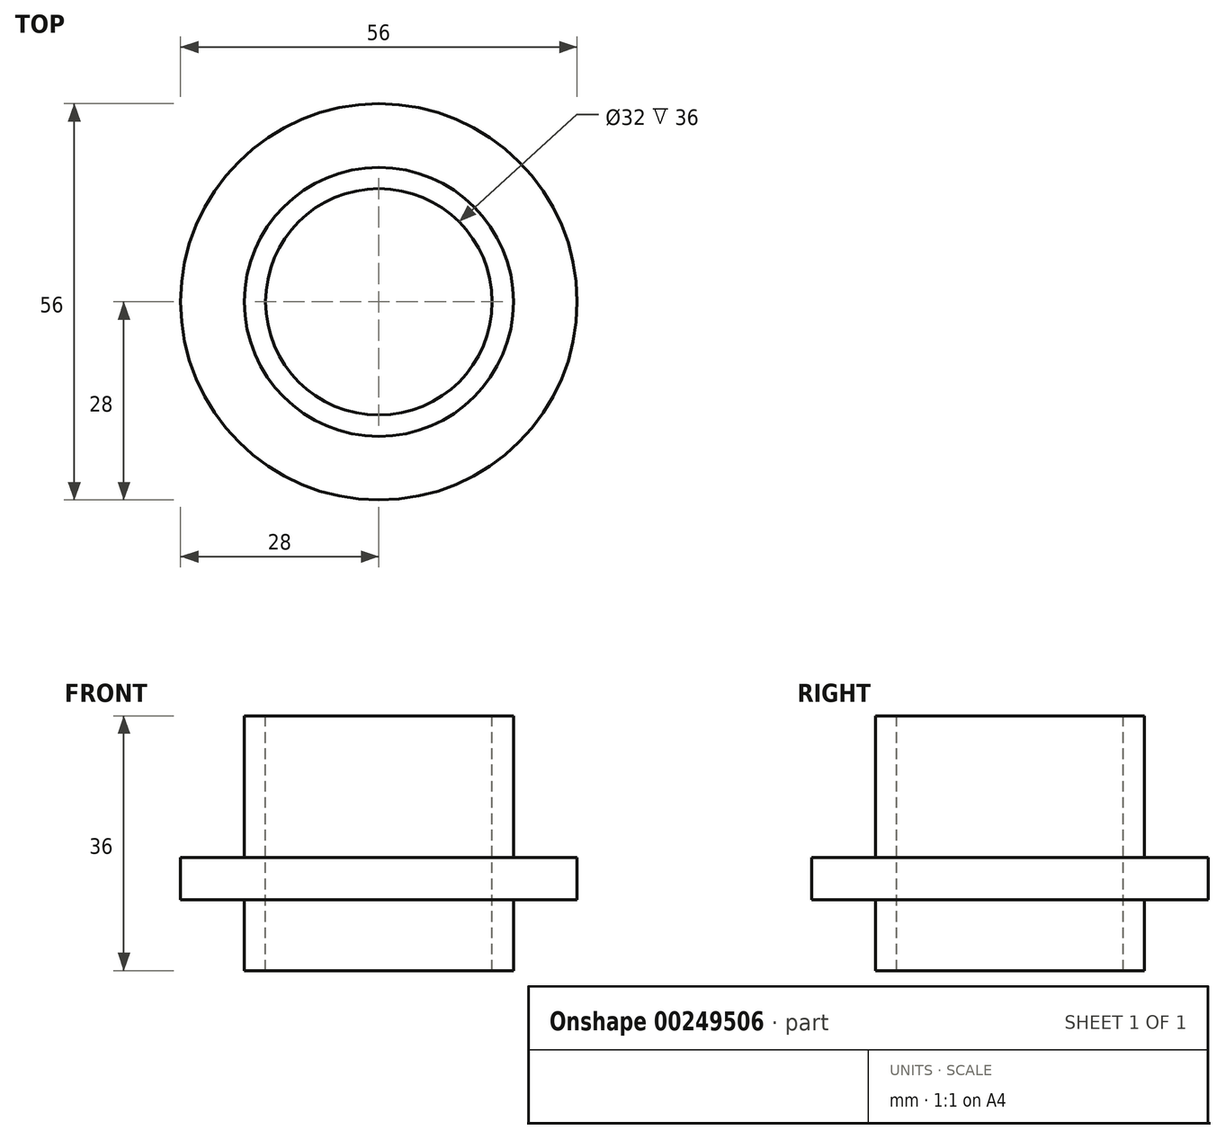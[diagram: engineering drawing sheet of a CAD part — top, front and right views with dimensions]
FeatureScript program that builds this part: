
annotation { "Feature Type Name" : "Feature", "Feature Type Description" : "" }
export const myFeature = defineFeature(function(context is Context, id is Id, definition is map)
    precondition{}
    {
        {
            var Q0;
            Q0=qCreatedBy(makeId("Top.planeOp"),FACE);
            var sketch = newSketch(context, id + "F0", { "sketchPlane" : qUnion([Q0])});
            skCircle(sketch, "E0", {"center": v(0, 0) * mm, "radius": 19 * mm});
            skSolve(sketch);
        }
        {
            var Q0;
            Q0=makeQuery(id+"F0.imprint","IMPRINT",FACE,{"disambiguationData":[TD([[makeQuery(id+"F0.imprint","IMPRINT",EDGE,{"derivedFrom":sQuery(id+"F0.wireOp",EDGE,"E0")}),1.0]])]});
            extrude(context, id + "F1", {"entities" : qUnion([Q0]), "oppositeDirection" : true, "depth" : 10 * mm});
        }
        {
            var Q0;
            Q0=makeQuery(id+"F1.opExtrude","CAP_FACE",FACE,{"disambiguationData":[OSD([sQuery(id+"F0.wireOp",EDGE,"E0")])],"isStart":true});
            var sketch = newSketch(context, id + "F2", { "sketchPlane" : qUnion([Q0])});
            skCircle(sketch, "E1", {"center": v(0, 0) * mm, "radius": 28 * mm});
            skSolve(sketch);
        }
        {
            var Q0;
            Q0 = qSketchRegion(id + "F2", true);
            extrude(context, id + "F3", {"entities" : qUnion([Q0]), "operationType" : NewBodyOperationType.ADD, "depth" : 6 * mm});
        }
        {
            var Q0;
            Q0=makeQuery(id+"F3.opExtrude","CAP_FACE",FACE,{"disambiguationData":[OSD([sQuery(id+"F2.wireOp",EDGE,"E1")])],"isStart":false});
            var sketch = newSketch(context, id + "F4", { "sketchPlane" : qUnion([Q0])});
            skCircle(sketch, "E2", {"center": v(0, 0) * mm, "radius": 19 * mm});
            skSolve(sketch);
        }
        {
            var Q0;
            Q0 = qSketchRegion(id + "F4", true);
            extrude(context, id + "F5", {"entities" : qUnion([Q0]), "operationType" : NewBodyOperationType.ADD, "depth" : 20 * mm});
        }
        {
            var Q0;
            Q0=makeQuery(id+"F5.opExtrude","CAP_FACE",FACE,{"disambiguationData":[OSD([sQuery(id+"F4.wireOp",EDGE,"E2")])],"isStart":false});
            var sketch = newSketch(context, id + "F6", { "sketchPlane" : qUnion([Q0])});
            skCircle(sketch, "E3", {"center": v(0, 0) * mm, "radius": 16 * mm});
            skSolve(sketch);
        }
        {
            var Q0;
            Q0 = qSketchRegion(id + "F6", true);
            extrude(context, id + "F7", {"entities" : qUnion([Q0]), "operationType" : NewBodyOperationType.REMOVE, "endBound" : BoundingType.THROUGH_ALL, "oppositeDirection" : true, "depth" : 25 * mm});
        }
    });
